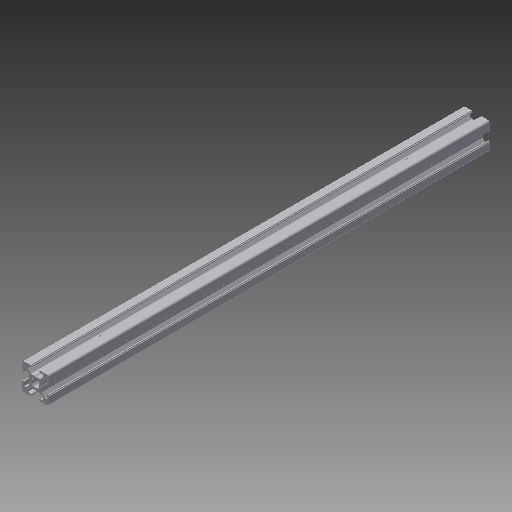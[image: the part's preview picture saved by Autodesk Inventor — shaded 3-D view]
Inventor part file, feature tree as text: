
AUTODESK INVENTOR PART (.ipt)
format: ipt  version: 2017 (Build 210142000, 142)  size: 405,504 bytes
history: native  units: in
note: dims shown in document units (in); Inventor stores cm internally (conversion verified against a paired STEP export)
features: other x3, sketch x2, extrude x1, hole x1, mirror x1
ambient origin geometry x8: Origin, YZ Plane, XZ Plane, XY Plane, X Axis, Y Axis, Z Axis, Center Point
bodies: Solid1 (feature_tree)
feature tree (8):
  other  "Blocks"
  extrude  "Extrusion1"  Depth=2.0in
  hole  "Hole1"  [1 undecoded]
  mirror  "Mirror1"
  sketch  "Sketch1"  dims[d1=0.0in d5=2.0in]
  other  "20x20"
  sketch  "Sketch3"  dims[d6=0.187in d7=0.75in d8=0.375in d9=0.25in d10=0.5635in d11=1.0in d12=0.8108in d13=1.0in d14=1.0in]
  other  "20x20:1"
note: 1 required parameter value undecoded (feature->parameter linkage not recoverable at this tier; creation-order binding heuristic only, values carry confidence <= 0.55)
